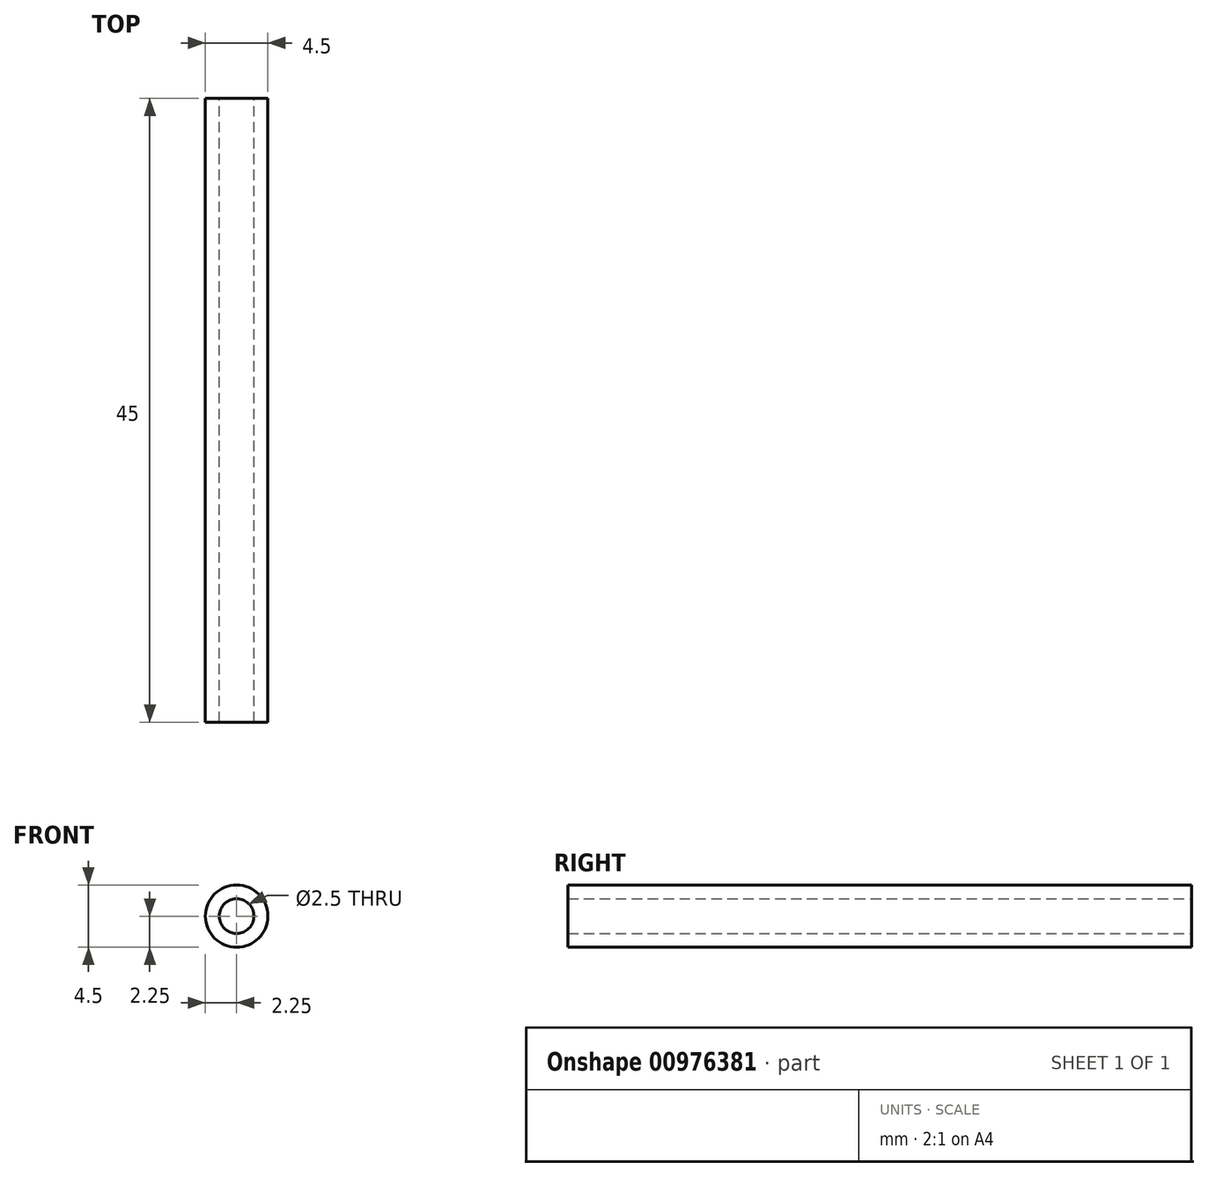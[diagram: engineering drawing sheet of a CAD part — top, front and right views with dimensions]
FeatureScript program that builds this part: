
annotation { "Feature Type Name" : "Feature", "Feature Type Description" : "" }
export const myFeature = defineFeature(function(context is Context, id is Id, definition is map)
    precondition{}
    {
        {
            var Q0;
            Q0=qCreatedBy(makeId("Front.planeOp"),FACE);
            var sketch = newSketch(context, id + "F0", { "sketchPlane" : qUnion([Q0])});
            skCircle(sketch, "E0", {"center": v(0, 0) * mm, "radius": 2.25 * mm});
            skCircle(sketch, "E1", {"center": v(0, 0) * mm, "radius": 1.25 * mm});
            skSolve(sketch);
        }
        {
            var Q0;
            Q0 = qSketchRegion(id + "F0", true);
            extrude(context, id + "F1", {"entities" : qUnion([Q0]), "depth" : 45 * mm, "offsetDistance" : 25 * mm});
        }
    });
